# Revit family: LCS-5_500
name_source: partatom
category: Generic Models
revit_build: Autodesk Revit 2017 (Build: 20170419_0315(x64)
units: mm (PartAtom-declared; Revit-internal decimal feet)

## family parameters
Always vertical = Yes
Can host rebar = No
Cut with Voids When Loaded = No
Host = Wall
Part Type = Normal
Room Calculation Point = No
Round Connector Dimension = Use Diameter
Shared = No

## types (1)
- 500
    Depth = 88 mm
    EAN = 4770046007641
    Height = 655 mm  [stored 2.14895 ft]
    Keynote = 6120
    LVI = 5489997
    Leveys = 500 mm  [stored 1.64042 ft]
    Manufacturer = Sentakia Oy
    Materiaali = kromattu messinki (CuZn36As)
    Model = LCS-5/500
    Sentakia_Material_Default = Stainless Steel, Polished_sentakia
    Teho = kromi: 117 W maalattu: 152 W
    URL = http//:www.sentakia.com

note: [stored X ft] marks values corroborated as IEEE doubles in the binary element streams (Revit-internal decimal feet)

## geometry (parser evidence)
native form markers: Blend x4, Sweep x2
no freeform markers — native parametric forms only
